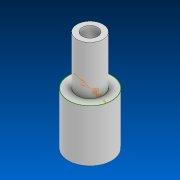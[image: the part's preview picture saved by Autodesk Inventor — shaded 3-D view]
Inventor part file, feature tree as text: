
AUTODESK INVENTOR PART (.ipt)
format: ipt  version: 2022 (Build 260153000, 153)  size: 94,720 bytes
history: native  units: in
note: dims shown in document units (in); Inventor stores cm internally (conversion verified against a paired STEP export)
features: extrude x2, sketch x1
ambient origin geometry x8: Origin, YZ Plane, XZ Plane, XY Plane, X Axis, Y Axis, Z Axis, Center Point
bodies: Solid1 (feature_tree)
feature tree (3):
  sketch  "Sketch1"  dims[d0=0.3in d1=0.18in d2=0.5in d3=0.6in d4=0.0in d5=0.56in d6=0.0in]
  extrude  "Extrusion1"  Depth=0.56in
  extrude  "Extrusion2"  Depth=0.56in
